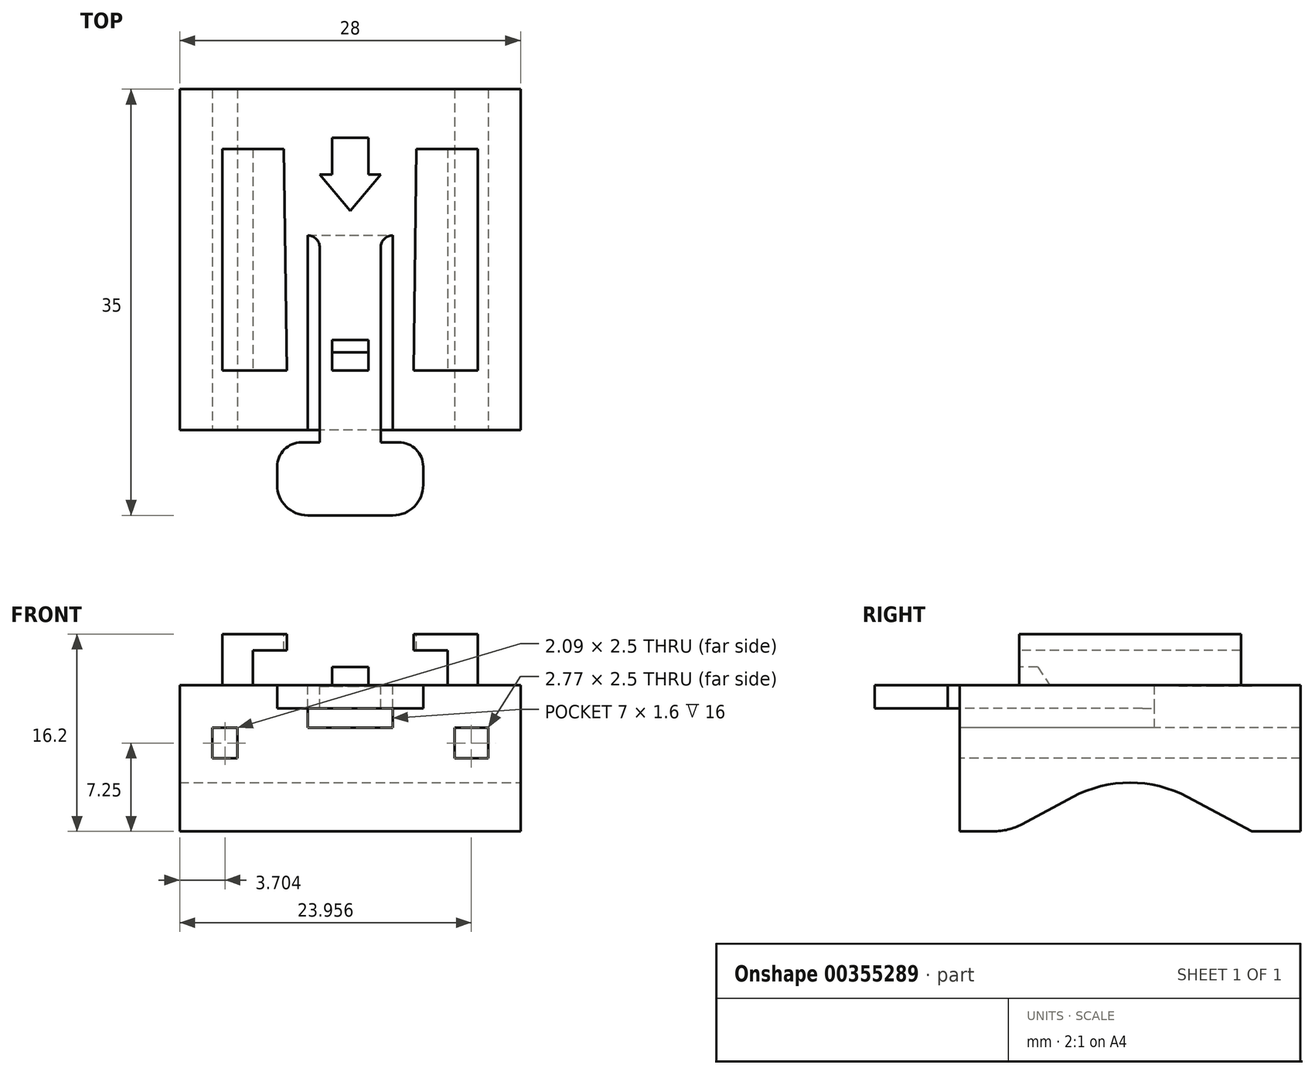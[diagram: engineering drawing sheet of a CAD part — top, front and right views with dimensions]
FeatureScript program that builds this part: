
annotation { "Feature Type Name" : "Feature", "Feature Type Description" : "" }
export const myFeature = defineFeature(function(context is Context, id is Id, definition is map)
    precondition{}
    {
        {
            var Q0;
            Q0=qCreatedBy(makeId("Front.planeOp"),FACE);
            var sketch = newSketch(context, id + "F0", { "sketchPlane" : qUnion([Q0])});
            skLineSegment(sketch, "E0.bottom", {"start": v(14, -6) * mm, "end": v(10, -6) * mm});
            skLineSegment(sketch, "E0.top", {"start": v(14, 6) * mm, "end": v(-14, 6) * mm});
            skLineSegment(sketch, "E0.left", {"start": v(14, -6) * mm, "end": v(14, 6) * mm});
            skLineSegment(sketch, "E0.right", {"start": v(-14, -6) * mm, "end": v(-14, 6) * mm});
            skPoint(sketch, "E0.middle", {"position": v(0, 0) * mm});
            skLineSegment(sketch, "E1", {"start": v(-10, -6) * mm, "end": v(-4.7, -3.18) * mm});
            skLineSegment(sketch, "E2.MirrorCS", {"start": v(10, -6) * mm, "end": v(4.7, -3.18) * mm});
            skPoint(sketch, "E3.visualSharp", {"position": v(0, -0.67) * mm});
            skArc(sketch, "E3.filletArc", {"start": v(4.7, -3.18) * mm, "mid": v(0, -2) * mm, "end": v(-4.7, -3.18) * mm});
            skLineSegment(sketch, "E4.trimOffspring", {"start": v(-10, -6) * mm, "end": v(-14, -6) * mm});
            skPoint(sketch, "E5.start.orphan", {"position": v(0, -2) * mm});
            skLineSegment(sketch, "E6", {"start": v(-10, -6) * mm, "end": v(10, -6) * mm});
            skSolve(sketch);
        }
        {
            var Q0;
            Q0=makeQuery(id+"F0.imprint","IMPRINT",FACE,{"disambiguationData":[TD([[makeQuery(id+"F0.imprint","IMPRINT",EDGE,{"derivedFrom":sQuery(id+"F0.wireOp",EDGE,"E0.bottom")}),-1.0]])]});
            var Q1;
            Q1=makeQuery(id+"F0.imprint","IMPRINT",FACE,{"disambiguationData":[TD([[makeQuery(id+"F0.imprint","IMPRINT",EDGE,{"derivedFrom":sQuery(id+"F0.wireOp",EDGE,"E1")}),-1.0]])]});
            extrude(context, id + "F1", {"entities" : qUnion([Q0, Q1]), "endBound" : BoundingType.SYMMETRIC, "depth" : 28 * mm});
        }
        {
            var Q0;
            Q0=qCreatedBy(makeId("Right.planeOp"),FACE);
            var sketch = newSketch(context, id + "F2", { "sketchPlane" : qUnion([Q0])});
            skLineSegment(sketch, "E7.bottom", {"start": v(14, -6) * mm, "end": v(10, -6) * mm});
            skLineSegment(sketch, "E7.top", {"start": v(14, 6) * mm, "end": v(-14, 6) * mm});
            skLineSegment(sketch, "E7.left", {"start": v(14, -6) * mm, "end": v(14, 6) * mm});
            skLineSegment(sketch, "E7.right", {"start": v(-14, -6) * mm, "end": v(-14, 6) * mm});
            skPoint(sketch, "E7.middle", {"position": v(0, 0) * mm});
            skLineSegment(sketch, "E8", {"start": v(-10, -6) * mm, "end": v(-4.7, -3.18) * mm});
            skLineSegment(sketch, "E9.MirrorCS", {"start": v(10, -6) * mm, "end": v(4.7, -3.18) * mm});
            skPoint(sketch, "E10.visualSharp", {"position": v(0, -0.67) * mm});
            skArc(sketch, "E10.filletArc", {"start": v(4.7, -3.18) * mm, "mid": v(0, -2) * mm, "end": v(-4.7, -3.18) * mm});
            skLineSegment(sketch, "E11.trimOffspring", {"start": v(-10, -6) * mm, "end": v(-14, -6) * mm});
            skPoint(sketch, "E12.start.orphan", {"position": v(0, -2) * mm});
            skPoint(sketch, "E13", {"position": v(0, 6) * mm});
            skLineSegment(sketch, "E14", {"start": v(-10, -6) * mm, "end": v(10, -6) * mm});
            skSolve(sketch);
        }
        {
            var Q0;
            Q0=makeQuery(id+"F1.opExtrude","CAP_FACE",FACE,{"disambiguationData":[OSD([sQuery(id+"F0.wireOp",EDGE,"E0.bottom"),sQuery(id+"F0.wireOp",EDGE,"E0.top"),sQuery(id+"F0.wireOp",EDGE,"E0.left"),sQuery(id+"F0.wireOp",EDGE,"E0.right"),sQuery(id+"F0.wireOp",EDGE,"E1"),sQuery(id+"F0.wireOp",EDGE,"E2.MirrorCS"),sQuery(id+"F0.wireOp",EDGE,"E3.filletArc"),sQuery(id+"F0.wireOp",EDGE,"E4.trimOffspring")])],"isStart":false});
            var sketch = newSketch(context, id + "F3", { "sketchPlane" : qUnion([Q0])});
            skLineSegment(sketch, "E15.bottom", {"start": v(3.5, 2.5) * mm, "end": v(-3.5, 2.5) * mm});
            skLineSegment(sketch, "E15.top", {"start": v(3.5, 6) * mm, "end": v(-3.5, 6) * mm});
            skLineSegment(sketch, "E15.left", {"start": v(3.5, 2.5) * mm, "end": v(3.5, 6) * mm});
            skLineSegment(sketch, "E15.right", {"start": v(-3.5, 2.5) * mm, "end": v(-3.5, 6) * mm});
            skPoint(sketch, "E15.middle", {"position": v(0, 4.25) * mm});
            skSolve(sketch);
        }
        {
            var Q0;
            Q0=makeQuery(id+"F3.imprint","IMPRINT",FACE,{"disambiguationData":[TD([[makeQuery(id+"F3.imprint","IMPRINT",EDGE,{"derivedFrom":sQuery(id+"F3.wireOp",EDGE,"E15.bottom")}),-1.0]])]});
            extrude(context, id + "F4", {"entities" : qUnion([Q0]), "operationType" : NewBodyOperationType.REMOVE, "oppositeDirection" : true, "depth" : 16 * mm});
        }
        {
            var Q0;
            Q0=makeQuery(id+"F1.opExtrude","SWEPT_FACE",FACE,{"disambiguationData":[OSD([sQuery(id+"F0.wireOp",EDGE,"E0.top")])]});
            var sketch = newSketch(context, id + "F5", { "sketchPlane" : qUnion([Q0])});
            skLineSegment(sketch, "E16.top", {"start": v(-2.5, -15) * mm, "end": v(2.5, -15) * mm});
            skLineSegment(sketch, "E16.left", {"start": v(-2.5, 2.41) * mm, "end": v(-2.5, -15) * mm});
            skLineSegment(sketch, "E16.right", {"start": v(2.5, 2.41) * mm, "end": v(2.5, -15) * mm});
            skLineSegment(sketch, "E17.bottom", {"start": v(3.5, -21) * mm, "end": v(-3.5, -21) * mm});
            skLineSegment(sketch, "E17.top", {"start": v(4, -15) * mm, "end": v(-4, -15) * mm});
            skLineSegment(sketch, "E17.left", {"start": v(6, -18.5) * mm, "end": v(6, -17) * mm});
            skLineSegment(sketch, "E17.right", {"start": v(-6, -18.5) * mm, "end": v(-6, -17) * mm});
            skPoint(sketch, "E17.middle", {"position": v(0, -18) * mm});
            skPoint(sketch, "E18.visualSharp", {"position": v(-6, -15) * mm});
            skArc(sketch, "E18.filletArc", {"start": v(-4, -15) * mm, "mid": v(-5.41, -15.59) * mm, "end": v(-6, -17) * mm});
            skPoint(sketch, "E19.visualSharp", {"position": v(-6, -21) * mm});
            skArc(sketch, "E19.filletArc", {"start": v(-6, -18.5) * mm, "mid": v(-5.27, -20.27) * mm, "end": v(-3.5, -21) * mm});
            skPoint(sketch, "E20.visualSharp", {"position": v(6, -21) * mm});
            skArc(sketch, "E20.filletArc", {"start": v(3.5, -21) * mm, "mid": v(5.27, -20.27) * mm, "end": v(6, -18.5) * mm});
            skPoint(sketch, "E21.visualSharp", {"position": v(6, -15) * mm});
            skArc(sketch, "E21.filletArc", {"start": v(6, -17) * mm, "mid": v(5.41, -15.59) * mm, "end": v(4, -15) * mm});
            skLineSegment(sketch, "E22", {"start": v(-2.5, 2.41) * mm, "end": v(2.5, 2.41) * mm});
            skSolve(sketch);
        }
        {
            var Q0;
            Q0=makeQuery(id+"F5.imprint","IMPRINT",FACE,{"disambiguationData":[TD([[makeQuery(id+"F5.imprint","IMPRINT",EDGE,{"derivedFrom":sQuery(id+"F5.wireOp",EDGE,"E17.bottom")}),-1.0]])]});
            var Q1;
            {var subQ1=sQuery(id+"F5.wireOp",EDGE,"E16.left");Q1=makeQuery(id+"F5.imprint","IMPRINT",FACE,{"disambiguationData":[TD([[makeQuery(id+"F5.imprint","IMPRINT",EDGE,{"derivedFrom":subQ1}),1.0]])]});}
            extrude(context, id + "F6", {"entities" : qUnion([Q0, Q1]), "oppositeDirection" : true, "depth" : 1.9 * mm});
        }
        {
            var Q0;
            Q0=makeQuery(id+"F6.opExtrude","SWEPT_BODY",BODY,{"disambiguationData":[OSD([sQuery(id+"F5.wireOp",EDGE,"E16.left"),sQuery(id+"F5.wireOp",EDGE,"E16.right"),sQuery(id+"F5.wireOp",EDGE,"E17.bottom"),sQuery(id+"F5.wireOp",EDGE,"E17.top"),sQuery(id+"F5.wireOp",EDGE,"E17.left"),sQuery(id+"F5.wireOp",EDGE,"E17.right"),sQuery(id+"F5.wireOp",EDGE,"E18.filletArc"),sQuery(id+"F5.wireOp",EDGE,"E19.filletArc"),sQuery(id+"F5.wireOp",EDGE,"E20.filletArc"),sQuery(id+"F5.wireOp",EDGE,"E21.filletArc"),sQuery(id+"F5.wireOp",EDGE,"E22")])]});
            var Q1;
            Q1=makeQuery(id+"F1.opExtrude","SWEPT_BODY",BODY,{"disambiguationData":[OSD([sQuery(id+"F0.wireOp",EDGE,"E0.bottom"),sQuery(id+"F0.wireOp",EDGE,"E0.top"),sQuery(id+"F0.wireOp",EDGE,"E0.left"),sQuery(id+"F0.wireOp",EDGE,"E0.right"),sQuery(id+"F0.wireOp",EDGE,"E1"),sQuery(id+"F0.wireOp",EDGE,"E2.MirrorCS"),sQuery(id+"F0.wireOp",EDGE,"E3.filletArc"),sQuery(id+"F0.wireOp",EDGE,"E4.trimOffspring")])]});
            booleanBodies(context, id + "F7", {"operationType" : BooleanOperationType.UNION, "tools" : qUnion([Q0, Q1])});
        }
        {
            var Q0;
            Q0=makeQuery(id+"F4.boolean.opBoolean","COPY",EDGE,{"derivedFrom":makeQuery(id+"F4.opExtrude","CAP_EDGE",EDGE,{"disambiguationData":[OSD([sQuery(id+"F3.wireOp",EDGE,"E15.right")])],"isStart":true})});
            var Q1;
            Q1=makeQuery(id+"F4.boolean.opBoolean","COPY",EDGE,{"derivedFrom":makeQuery(id+"F4.opExtrude","CAP_EDGE",EDGE,{"disambiguationData":[OSD([sQuery(id+"F3.wireOp",EDGE,"E15.left")])],"isStart":true})});
            var Q2;
            Q2=makeQuery(id+"F7.opBoolean","INTERSECT",EDGE,{"derivedFrom":[makeQuery(id+"F4.boolean.opBoolean","COPY",FACE,{"derivedFrom":makeQuery(id+"F4.opExtrude","CAP_FACE",FACE,{"disambiguationData":[OSD([sQuery(id+"F3.wireOp",EDGE,"E15.bottom"),sQuery(id+"F3.wireOp",EDGE,"E15.top"),sQuery(id+"F3.wireOp",EDGE,"E15.left"),sQuery(id+"F3.wireOp",EDGE,"E15.right")])],"isStart":false})}),makeQuery(id+"F6.opExtrude","SWEPT_FACE",FACE,{"disambiguationData":[OSD([sQuery(id+"F5.wireOp",EDGE,"E16.right")])]})]});
            var Q3;
            Q3=makeQuery(id+"F7.opBoolean","INTERSECT",EDGE,{"derivedFrom":[makeQuery(id+"F4.boolean.opBoolean","COPY",FACE,{"derivedFrom":makeQuery(id+"F4.opExtrude","CAP_FACE",FACE,{"disambiguationData":[OSD([sQuery(id+"F3.wireOp",EDGE,"E15.bottom"),sQuery(id+"F3.wireOp",EDGE,"E15.top"),sQuery(id+"F3.wireOp",EDGE,"E15.left"),sQuery(id+"F3.wireOp",EDGE,"E15.right")])],"isStart":false})}),makeQuery(id+"F6.opExtrude","SWEPT_FACE",FACE,{"disambiguationData":[OSD([sQuery(id+"F5.wireOp",EDGE,"E16.left")])]})]});
            fillet(context, id + "F8", {"entities" : qUnion([Q0, Q1, Q2, Q3]), "radius" : 1 * mm, "tangentPropagation" : true, "allowEdgeOverflow" : false});
        }
        {
            var Q0;
            Q0=qCreatedBy(makeId("Right.planeOp"),FACE);
            var sketch = newSketch(context, id + "F9", { "sketchPlane" : qUnion([Q0])});
            skLineSegment(sketch, "E23.bottom", {"start": v(-7.6, 7.5) * mm, "end": v(-9.1, 7.5) * mm});
            skLineSegment(sketch, "E23.top", {"start": v(-6.6, 6) * mm, "end": v(-9.1, 6) * mm});
            skLineSegment(sketch, "E23.right", {"start": v(-9.1, 7.5) * mm, "end": v(-9.1, 6) * mm});
            skLineSegment(sketch, "E24", {"start": v(-7.6, 7.5) * mm, "end": v(-6.6, 6) * mm});
            skSolve(sketch);
        }
        {
            var Q0;
            Q0=makeQuery(id+"F9.imprint","IMPRINT",FACE,{"disambiguationData":[TD([[makeQuery(id+"F9.imprint","IMPRINT",EDGE,{"derivedFrom":sQuery(id+"F9.wireOp",EDGE,"E23.bottom")}),1.0]])]});
            extrude(context, id + "F10", {"entities" : qUnion([Q0]), "operationType" : NewBodyOperationType.ADD, "endBound" : BoundingType.SYMMETRIC, "depth" : 3 * mm});
        }
        {
            var Q0;
            Q0=makeQuery(id+"F7.opBoolean","MERGE",FACE,{"derivedFrom":[makeQuery(id+"F1.opExtrude","SWEPT_FACE",FACE,{"disambiguationData":[OSD([sQuery(id+"F0.wireOp",EDGE,"E0.top")])]}),makeQuery(id+"F6.opExtrude","CAP_FACE",FACE,{"disambiguationData":[OSD([sQuery(id+"F5.wireOp",EDGE,"E16.left"),sQuery(id+"F5.wireOp",EDGE,"E16.right"),sQuery(id+"F5.wireOp",EDGE,"E17.bottom"),sQuery(id+"F5.wireOp",EDGE,"E17.top"),sQuery(id+"F5.wireOp",EDGE,"E17.left"),sQuery(id+"F5.wireOp",EDGE,"E17.right"),sQuery(id+"F5.wireOp",EDGE,"E18.filletArc"),sQuery(id+"F5.wireOp",EDGE,"E19.filletArc"),sQuery(id+"F5.wireOp",EDGE,"E20.filletArc"),sQuery(id+"F5.wireOp",EDGE,"E21.filletArc"),sQuery(id+"F5.wireOp",EDGE,"E22")])],"isStart":true})]});
            var sketch = newSketch(context, id + "F11", { "sketchPlane" : qUnion([Q0])});
            skLineSegment(sketch, "E25.bottom", {"start": v(-8, 9.1) * mm, "end": v(-10.5, 9.1) * mm});
            skLineSegment(sketch, "E25.top", {"start": v(-8, -9.1) * mm, "end": v(-10.5, -9.1) * mm});
            skLineSegment(sketch, "E25.left", {"start": v(-8, 9.1) * mm, "end": v(-8, -9.1) * mm});
            skLineSegment(sketch, "E25.right", {"start": v(-10.5, 9.1) * mm, "end": v(-10.5, -9.1) * mm});
            skPoint(sketch, "E25.middle", {"position": v(-9.25, 0) * mm});
            skLineSegment(sketch, "E26.MirrorCS", {"start": v(8, -9.1) * mm, "end": v(10.5, -9.1) * mm});
            skPoint(sketch, "E27.MirrorP", {"position": v(9.25, 0) * mm});
            skLineSegment(sketch, "E28.MirrorCS", {"start": v(8, 9.1) * mm, "end": v(8, -9.1) * mm});
            skLineSegment(sketch, "E29.MirrorCS", {"start": v(10.5, 9.1) * mm, "end": v(10.5, -9.1) * mm});
            skLineSegment(sketch, "E30.MirrorCS", {"start": v(8, 9.1) * mm, "end": v(10.5, 9.1) * mm});
            skSolve(sketch);
        }
        {
            var Q0;
            Q0=makeQuery(id+"F11.imprint","IMPRINT",FACE,{"disambiguationData":[TD([[makeQuery(id+"F11.imprint","IMPRINT",EDGE,{"derivedFrom":sQuery(id+"F11.wireOp",EDGE,"E25.bottom")}),1.0]])]});
            var Q1;
            Q1=makeQuery(id+"F11.imprint","IMPRINT",FACE,{"disambiguationData":[TD([[makeQuery(id+"F11.imprint","IMPRINT",EDGE,{"derivedFrom":sQuery(id+"F11.wireOp",EDGE,"E26.MirrorCS")}),1.0]])]});
            extrude(context, id + "F12", {"entities" : qUnion([Q0, Q1]), "operationType" : NewBodyOperationType.ADD, "depth" : 4.2 * mm});
        }
        {
            var Q0;
            Q0=makeQuery(id+"F12.opExtrude","CAP_FACE",FACE,{"disambiguationData":[OSD([sQuery(id+"F11.wireOp",EDGE,"E25.bottom"),sQuery(id+"F11.wireOp",EDGE,"E25.top"),sQuery(id+"F11.wireOp",EDGE,"E25.left"),sQuery(id+"F11.wireOp",EDGE,"E25.right")])],"isStart":false});
            var sketch = newSketch(context, id + "F13", { "sketchPlane" : qUnion([Q0])});
            skLineSegment(sketch, "E31", {"start": v(-10.5, 9.1) * mm, "end": v(-10.5, -9.1) * mm});
            skLineSegment(sketch, "E32", {"start": v(-10.5, 9.1) * mm, "end": v(-5.45, 9.1) * mm});
            skLineSegment(sketch, "E33", {"start": v(-5.45, 9.1) * mm, "end": v(-5.2, -9.1) * mm});
            skLineSegment(sketch, "E34", {"start": v(-5.2, -9.1) * mm, "end": v(-10.5, -9.1) * mm});
            skLineSegment(sketch, "E35.MirrorCS", {"start": v(5.2, -9.1) * mm, "end": v(10.5, -9.1) * mm});
            skLineSegment(sketch, "E36.MirrorCS", {"start": v(5.45, 9.1) * mm, "end": v(5.2, -9.1) * mm});
            skLineSegment(sketch, "E37.MirrorCS", {"start": v(10.5, 9.1) * mm, "end": v(10.5, -9.1) * mm});
            skLineSegment(sketch, "E38.MirrorCS", {"start": v(10.5, 9.1) * mm, "end": v(5.45, 9.1) * mm});
            skSolve(sketch);
        }
        {
            var Q0;
            {var subQ0=sQuery(id+"F13.wireOp",EDGE,"E31");Q0=makeQuery(id+"F13.imprint","IMPRINT",FACE,{"disambiguationData":[TD([[makeQuery(id+"F13.imprint","IMPRINT",EDGE,{"derivedFrom":subQ0}),1.0]])]});}
            var Q1;
            {var subQ2=sQuery(id+"F13.wireOp",EDGE,"E33");Q1=makeQuery(id+"F13.imprint","IMPRINT",FACE,{"disambiguationData":[TD([[makeQuery(id+"F13.imprint","IMPRINT",EDGE,{"derivedFrom":subQ2}),-1.0]])]});}
            var Q2;
            Q2=makeQuery(id+"F13.imprint","IMPRINT",FACE,{"disambiguationData":[TD([[makeQuery(id+"F13.imprint","IMPRINT",EDGE,{"derivedFrom":sQuery(id+"F13.wireOp",EDGE,"E35.MirrorCS")}),1.0]])]});
            extrude(context, id + "F14", {"entities" : qUnion([Q0, Q1, Q2]), "operationType" : NewBodyOperationType.ADD, "oppositeDirection" : true, "depth" : 1.35 * mm});
        }
        {
            var Q0;
            Q0=makeQuery(id+"F7.opBoolean","MERGE",FACE,{"derivedFrom":[makeQuery(id+"F1.opExtrude","SWEPT_FACE",FACE,{"disambiguationData":[OSD([sQuery(id+"F0.wireOp",EDGE,"E0.top")])]}),makeQuery(id+"F6.opExtrude","CAP_FACE",FACE,{"disambiguationData":[OSD([sQuery(id+"F5.wireOp",EDGE,"E16.left"),sQuery(id+"F5.wireOp",EDGE,"E16.right"),sQuery(id+"F5.wireOp",EDGE,"E17.bottom"),sQuery(id+"F5.wireOp",EDGE,"E17.top"),sQuery(id+"F5.wireOp",EDGE,"E17.left"),sQuery(id+"F5.wireOp",EDGE,"E17.right"),sQuery(id+"F5.wireOp",EDGE,"E18.filletArc"),sQuery(id+"F5.wireOp",EDGE,"E19.filletArc"),sQuery(id+"F5.wireOp",EDGE,"E20.filletArc"),sQuery(id+"F5.wireOp",EDGE,"E21.filletArc"),sQuery(id+"F5.wireOp",EDGE,"E22")])],"isStart":true})]});
            var sketch = newSketch(context, id + "F15", { "sketchPlane" : qUnion([Q0])});
            skLineSegment(sketch, "E39.bottom", {"start": v(1.5, 10) * mm, "end": v(-1.5, 10) * mm});
            skLineSegment(sketch, "E39.top", {"start": v(1.5, 7) * mm, "end": v(-1.5, 7) * mm});
            skLineSegment(sketch, "E39.left", {"start": v(1.5, 10) * mm, "end": v(1.5, 7) * mm});
            skLineSegment(sketch, "E39.right", {"start": v(-1.5, 10) * mm, "end": v(-1.5, 7) * mm});
            skPoint(sketch, "E39.middle", {"position": v(0, 8.5) * mm});
            skLineSegment(sketch, "E40", {"start": v(-1.5, 7) * mm, "end": v(-2.5, 7) * mm});
            skLineSegment(sketch, "E41", {"start": v(-2.5, 7) * mm, "end": v(0, 4) * mm});
            skLineSegment(sketch, "E42", {"start": v(1.5, 7) * mm, "end": v(2.5, 7) * mm});
            skLineSegment(sketch, "E43", {"start": v(0, 4) * mm, "end": v(2.5, 7) * mm});
            skSolve(sketch);
        }
        {
            var Q0;
            Q0=makeQuery(id+"F15.imprint","IMPRINT",FACE,{"disambiguationData":[TD([[makeQuery(id+"F15.imprint","IMPRINT",EDGE,{"derivedFrom":sQuery(id+"F15.wireOp",EDGE,"E39.bottom")}),1.0]])]});
            var Q1;
            Q1=makeQuery(id+"F15.imprint","IMPRINT",FACE,{"disambiguationData":[TD([[makeQuery(id+"F15.imprint","IMPRINT",EDGE,{"derivedFrom":sQuery(id+"F15.wireOp",EDGE,"E39.top")}),1.0]])]});
            extrude(context, id + "F16", {"entities" : qUnion([Q0, Q1]), "operationType" : NewBodyOperationType.REMOVE, "oppositeDirection" : true, "depth" : .1 * mm});
        }
        {
            var Q0;
            Q0=makeQuery(id+"F2.imprint","IMPRINT",FACE,{"disambiguationData":[TD([[makeQuery(id+"F2.imprint","IMPRINT",EDGE,{"derivedFrom":sQuery(id+"F2.wireOp",EDGE,"E8")}),-1.0]])]});
            extrude(context, id + "F17", {"entities" : qUnion([Q0]), "operationType" : NewBodyOperationType.REMOVE, "endBound" : BoundingType.SYMMETRIC, "oppositeDirection" : true, "depth" : 30 * mm});
        }
        {
            var Q0;
            Q0=makeQuery(id+"F17.boolean.opBoolean","COPY",EDGE,{"derivedFrom":makeQuery(id+"F17.opExtrude","SWEPT_EDGE",EDGE,{"disambiguationData":[OSD([sQuery(id+"F2.wireOp",EDGE,"E8"),sQuery(id+"F2.wireOp",EDGE,"E11.trimOffspring"),sQuery(id+"F2.wireOp",EDGE,"E14")])]})});
            var Q1;
            Q1=makeQuery(id+"F17.boolean.opBoolean","COPY",EDGE,{"derivedFrom":makeQuery(id+"F17.opExtrude","SWEPT_EDGE",EDGE,{"disambiguationData":[OSD([sQuery(id+"F2.wireOp",EDGE,"E7.bottom"),sQuery(id+"F2.wireOp",EDGE,"E9.MirrorCS"),sQuery(id+"F2.wireOp",EDGE,"E14")])]})});
            fillet(context, id + "F18", {"entities" : qUnion([Q0, Q1]), "radius" : 5 * mm, "tangentPropagation" : true, "allowEdgeOverflow" : false});
        }
        {
            var Q0;
            Q0=makeQuery(id+"F1.opExtrude","CAP_FACE",FACE,{"disambiguationData":[OSD([sQuery(id+"F0.wireOp",EDGE,"E0.bottom"),sQuery(id+"F0.wireOp",EDGE,"E0.top"),sQuery(id+"F0.wireOp",EDGE,"E0.left"),sQuery(id+"F0.wireOp",EDGE,"E0.right"),sQuery(id+"F0.wireOp",EDGE,"E4.trimOffspring"),sQuery(id+"F0.wireOp",EDGE,"E6")])],"isStart":false});
            var sketch = newSketch(context, id + "F19", { "sketchPlane" : qUnion([Q0])});
            skPoint(sketch, "E44.firstSnap0", {"position": v(0, 2.5) * mm});
            skPoint(sketch, "E44.oppositeSnap0", {"position": v(-9.25, 6) * mm});
            skLineSegment(sketch, "E44.bottom", {"start": v(-11.34, 2.5) * mm, "end": v(-9.25, 2.5) * mm});
            skLineSegment(sketch, "E44.top", {"start": v(-11.34, 0) * mm, "end": v(-9.25, 0) * mm});
            skLineSegment(sketch, "E44.left", {"start": v(-11.34, 2.5) * mm, "end": v(-11.34, 0) * mm});
            skLineSegment(sketch, "E44.right", {"start": v(-9.25, 2.5) * mm, "end": v(-9.25, 0) * mm});
            skLineSegment(sketch, "E45.bottom", {"start": v(8.57, 0) * mm, "end": v(11.34, 0) * mm});
            skLineSegment(sketch, "E45.top", {"start": v(8.57, 2.5) * mm, "end": v(11.34, 2.5) * mm});
            skLineSegment(sketch, "E45.left", {"start": v(8.57, 0) * mm, "end": v(8.57, 2.5) * mm});
            skLineSegment(sketch, "E45.right", {"start": v(11.34, 0) * mm, "end": v(11.34, 2.5) * mm});
            skLineSegment(sketch, "E46.bottom", {"start": v(-9.25, 2.5) * mm, "end": v(-7.3, 2.5) * mm});
            skLineSegment(sketch, "E46.top", {"start": v(-9.25, 2.5) * mm, "end": v(-7.3, 2.5) * mm});
            skLineSegment(sketch, "E46.left", {"start": v(-9.25, 2.5) * mm, "end": v(-9.25, 2.5) * mm});
            skLineSegment(sketch, "E46.right", {"start": v(-7.3, 2.5) * mm, "end": v(-7.3, 2.5) * mm});
            skSolve(sketch);
        }
        {
            var Q0;
            Q0=makeQuery(id+"F19.imprint","IMPRINT",FACE,{"disambiguationData":[TD([[makeQuery(id+"F19.imprint","IMPRINT",EDGE,{"derivedFrom":sQuery(id+"F19.wireOp",EDGE,"E44.bottom")}),-1.0]])]});
            extrude(context, id + "F20", {"entities" : qUnion([Q0]), "operationType" : NewBodyOperationType.REMOVE, "endBound" : BoundingType.THROUGH_ALL, "oppositeDirection" : true, "depth" : 25 * mm});
        }
        {
            var Q0;
            Q0 = qSketchRegion(id + "F19", true);
            extrude(context, id + "F21", {"entities" : qUnion([Q0]), "operationType" : NewBodyOperationType.REMOVE, "endBound" : BoundingType.THROUGH_ALL, "oppositeDirection" : true, "depth" : 25 * mm});
        }
        {
            var Q0;
            Q0=makeQuery(id+"F1.opExtrude","SWEPT_FACE",FACE,{"disambiguationData":[OSD([sQuery(id+"F0.wireOp",EDGE,"E0.left")])]});
            var sketch = newSketch(context, id + "F22", { "sketchPlane" : qUnion([Q0])});
            skText(sketch, "E47", { "text": "Ozzies", "fontName": "NotoSansCJKjp-Regular.otf"});
            const initialGuessF22  = {"E47": [-0.00675, 0.00026, 1, 0, 0.00325]};
            skSetInitialGuess(sketch, initialGuessF22);
            skSolve(sketch);
        }
        {
            var Q0;
            Q0 = qConstructionFilter(qBodyType(qCreatedBy(id + "F22" ,EDGE), BodyType.WIRE), ConstructionObject.NO);
            extrude(context, id + "F23", {"bodyType" : ToolBodyType.SURFACE, "operationType" : NewBodyOperationType.REMOVE, "surfaceEntities" : qUnion([Q0]), "oppositeDirection" : true, "depth" : 0.5 * mm, "hasDraft" : true, "draftAngle" : 3 * degree});
        }
    });
